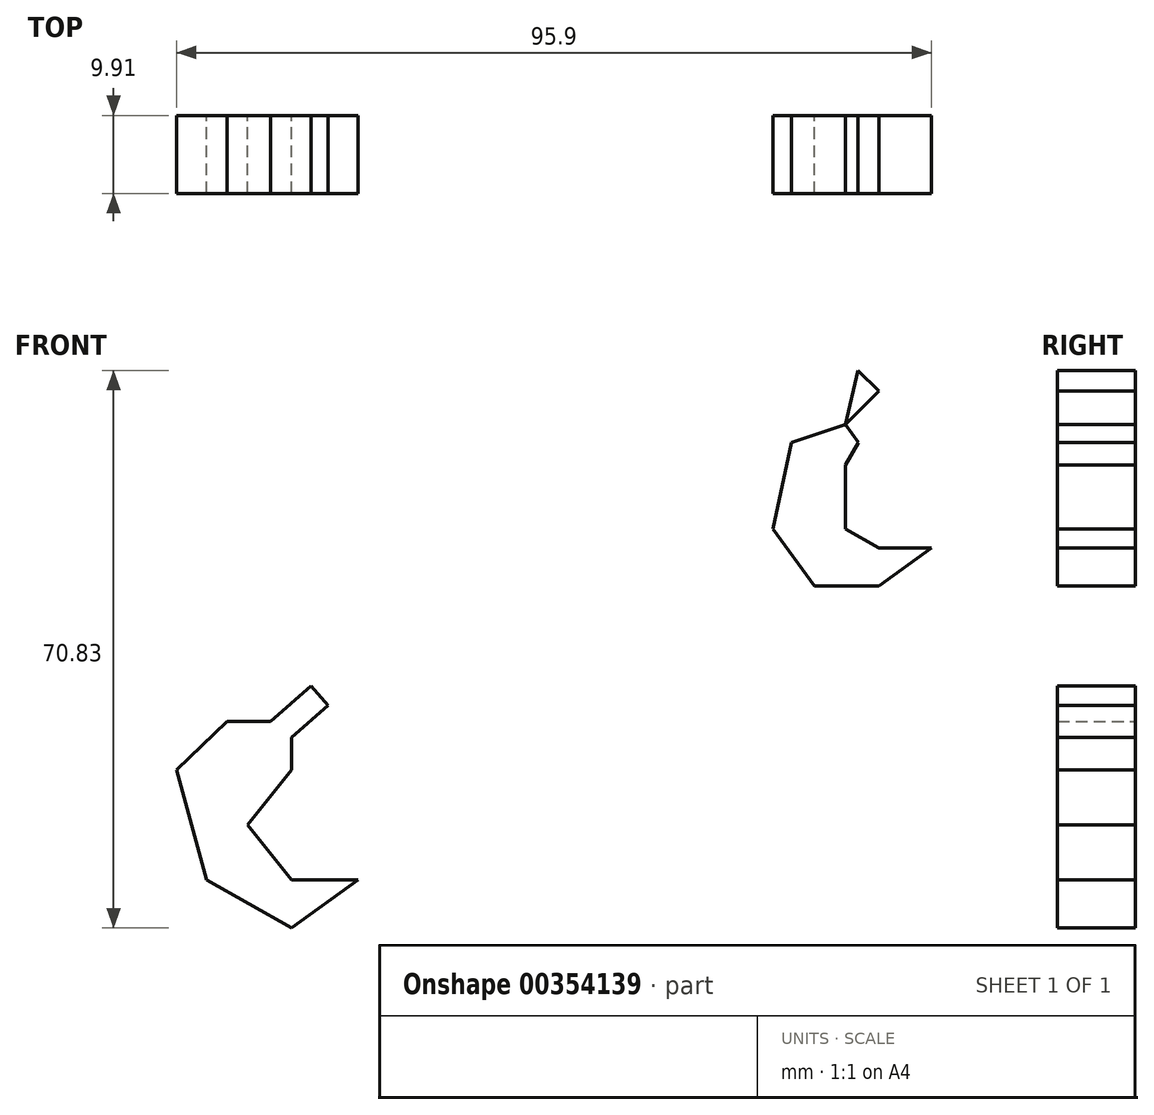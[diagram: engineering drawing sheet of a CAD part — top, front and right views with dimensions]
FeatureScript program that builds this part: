
annotation { "Feature Type Name" : "Feature", "Feature Type Description" : "" }
export const myFeature = defineFeature(function(context is Context, id is Id, definition is map)
    precondition{}
    {
        {
            var Q0;
            Q0=qCreatedBy(makeId("Front.planeOp"),FACE);
            var sketch = newSketch(context, id + "F0", { "sketchPlane" : qUnion([Q0])});
            skLineSegment(sketch, "E0", {"start": v(-20.4, -24.63) * mm, "end": v(-28.86, -24.63) * mm});
            skLineSegment(sketch, "E1", {"start": v(-28.86, -24.63) * mm, "end": v(-34.4, -17.63) * mm});
            skLineSegment(sketch, "E2", {"start": v(-34.4, -17.63) * mm, "end": v(-28.86, -10.64) * mm});
            skLineSegment(sketch, "E3", {"start": v(-28.86, -10.64) * mm, "end": v(-28.86, -6.56) * mm});
            skLineSegment(sketch, "E4", {"start": v(-28.86, -6.56) * mm, "end": v(-24.2, -2.48) * mm});
            skLineSegment(sketch, "E5", {"start": v(-24.2, -2.48) * mm, "end": v(-26.36, 0) * mm});
            skLineSegment(sketch, "E6", {"start": v(-26.36, 0) * mm, "end": v(-31.52, -4.51) * mm});
            skLineSegment(sketch, "E7", {"start": v(-31.52, -4.51) * mm, "end": v(-37.02, -4.51) * mm});
            skLineSegment(sketch, "E8", {"start": v(-37.02, -4.51) * mm, "end": v(-43.43, -10.64) * mm});
            skLineSegment(sketch, "E9", {"start": v(-43.43, -10.64) * mm, "end": v(-39.64, -24.63) * mm});
            skLineSegment(sketch, "E10", {"start": v(-39.64, -24.63) * mm, "end": v(-28.86, -30.75) * mm});
            skLineSegment(sketch, "E11", {"start": v(-28.86, -30.75) * mm, "end": v(-20.4, -24.63) * mm});
            skLineSegment(sketch, "E12", {"start": v(43.14, 40.08) * mm, "end": v(45.76, 37.45) * mm});
            skLineSegment(sketch, "E13", {"start": v(45.76, 37.45) * mm, "end": v(41.54, 33.23) * mm});
            skLineSegment(sketch, "E14", {"start": v(41.54, 33.23) * mm, "end": v(43.18, 30.96) * mm});
            skLineSegment(sketch, "E15", {"start": v(43.18, 30.96) * mm, "end": v(41.54, 28.07) * mm});
            skLineSegment(sketch, "E16", {"start": v(41.54, 28.07) * mm, "end": v(41.54, 19.97) * mm});
            skLineSegment(sketch, "E17", {"start": v(41.54, 19.97) * mm, "end": v(45.76, 17.57) * mm});
            skLineSegment(sketch, "E18", {"start": v(45.76, 17.57) * mm, "end": v(52.47, 17.57) * mm});
            skLineSegment(sketch, "E19", {"start": v(52.47, 17.57) * mm, "end": v(45.76, 12.71) * mm});
            skLineSegment(sketch, "E20", {"start": v(45.76, 12.71) * mm, "end": v(37.6, 12.71) * mm});
            skLineSegment(sketch, "E21", {"start": v(37.6, 12.71) * mm, "end": v(32.35, 19.97) * mm});
            skLineSegment(sketch, "E22", {"start": v(32.35, 19.97) * mm, "end": v(34.69, 30.96) * mm});
            skLineSegment(sketch, "E23", {"start": v(34.69, 30.96) * mm, "end": v(41.54, 33.23) * mm});
            skLineSegment(sketch, "E24", {"start": v(43.14, 40.08) * mm, "end": v(41.54, 33.23) * mm});
            skSolve(sketch);
        }
        {
            var Q0;
            Q0 = qSketchRegion(id + "F0", true);
            extrude(context, id + "F1", {"entities" : qUnion([Q0]), "depth" : 9.9 * mm});
        }
    });
